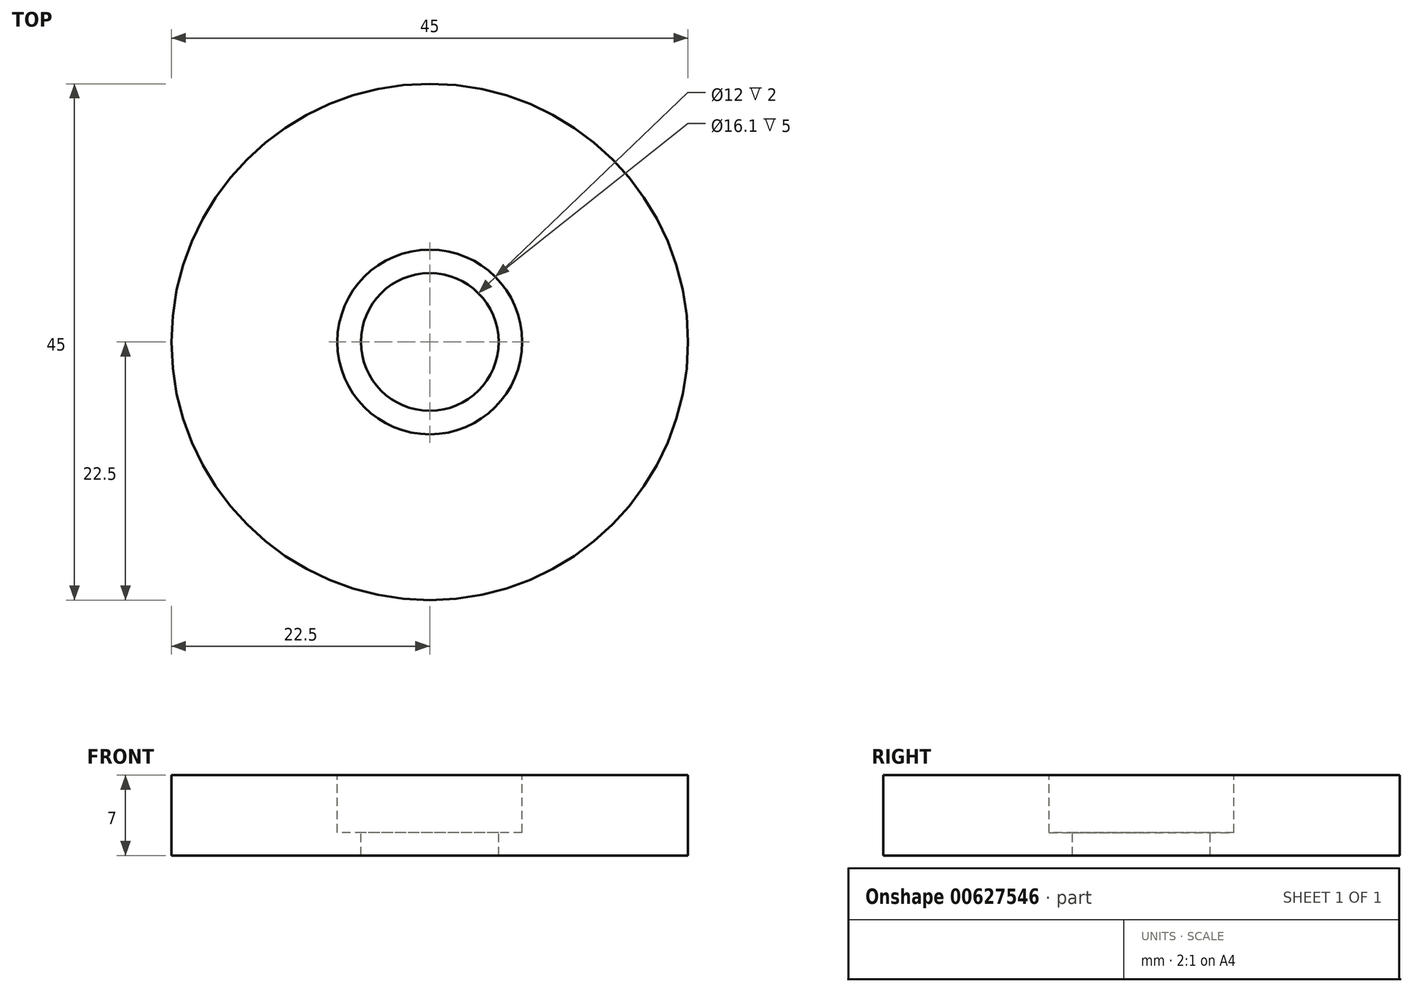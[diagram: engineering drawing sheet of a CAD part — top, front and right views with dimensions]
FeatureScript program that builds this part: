
annotation { "Feature Type Name" : "Feature", "Feature Type Description" : "" }
export const myFeature = defineFeature(function(context is Context, id is Id, definition is map)
    precondition{}
    {
        {
            var Q0;
            Q0=qCreatedBy(makeId("Top.planeOp"),FACE);
            var sketch = newSketch(context, id + "F0", { "sketchPlane" : qUnion([Q0])});
            skCircle(sketch, "E0", {"center": v(0, 0) * mm, "radius": 22.5 * mm});
            skSolve(sketch);
        }
        {
            var Q0;
            Q0 = qSketchRegion(id + "F0", true);
            extrude(context, id + "F1", {"entities" : qUnion([Q0]), "depth" : 7 * mm, "offsetDistance" : 25 * mm});
        }
        {
            var Q0;
            Q0=makeQuery(id+"F1.opExtrude","CAP_FACE",FACE,{"disambiguationData":[OSD([sQuery(id+"F0.wireOp",EDGE,"E0")])],"isStart":false});
            var sketch = newSketch(context, id + "F2", { "sketchPlane" : qUnion([Q0])});
            skCircle(sketch, "E1", {"center": v(0, 0) * mm, "radius": 6 * mm});
            skSolve(sketch);
        }
        {
            var Q0;
            Q0 = qSketchRegion(id + "F2", true);
            extrude(context, id + "F3", {"entities" : qUnion([Q0]), "operationType" : NewBodyOperationType.REMOVE, "endBound" : BoundingType.THROUGH_ALL, "oppositeDirection" : true, "depth" : 25 * mm, "offsetDistance" : 25 * mm});
        }
        {
            var Q0;
            Q0=makeQuery(id+"F1.opExtrude","CAP_FACE",FACE,{"disambiguationData":[OSD([sQuery(id+"F0.wireOp",EDGE,"E0")])],"isStart":false});
            var sketch = newSketch(context, id + "F4", { "sketchPlane" : qUnion([Q0])});
            skCircle(sketch, "E2", {"center": v(0, 0) * mm, "radius": 8.05 * mm});
            skSolve(sketch);
        }
        {
            var Q0;
            Q0 = qSketchRegion(id + "F4", true);
            extrude(context, id + "F5", {"entities" : qUnion([Q0]), "operationType" : NewBodyOperationType.REMOVE, "oppositeDirection" : true, "depth" : 5 * mm, "offsetDistance" : 25 * mm});
        }
    });
